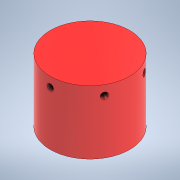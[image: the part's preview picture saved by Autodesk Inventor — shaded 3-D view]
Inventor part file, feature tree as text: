
AUTODESK INVENTOR PART (.ipt)
format: ipt  version: 2021 (Build 250183000, 183)  size: 133,632 bytes
history: native  units: mm
features: sketch x2, revolve x1, extrude x1, thread x1, pattern_circular x1
ambient origin geometry x8: Origin, YZ Plane, XZ Plane, XY Plane, X Axis, Y Axis, Z Axis, Center Point
bodies: Solid1 (feature_tree)
feature tree (6):
  revolve  "Revolution1"  [1 undecoded]
  extrude  "Extrusion1"  Depth=34.0mm
  thread  "Thread1"  [1 undecoded]
  pattern_circular  "Circular Pattern1"  [2 undecoded]
  sketch  "Sketch1"  dims[d0=40.0mm d1=20.0mm]
  sketch  "Sketch2"  dims[d2=0.0mm d3=13.335mm d4=0.0mm d5=25.0mm d6=90.0deg d7=4.0mm d8=34.0mm d9=20.0mm d10=0.0mm d11=20.08mm d12=0.0mm d13=60.0mm d14=360.0deg]
note: 4 required parameter values undecoded (feature->parameter linkage not recoverable at this tier; creation-order binding heuristic only, values carry confidence <= 0.55)